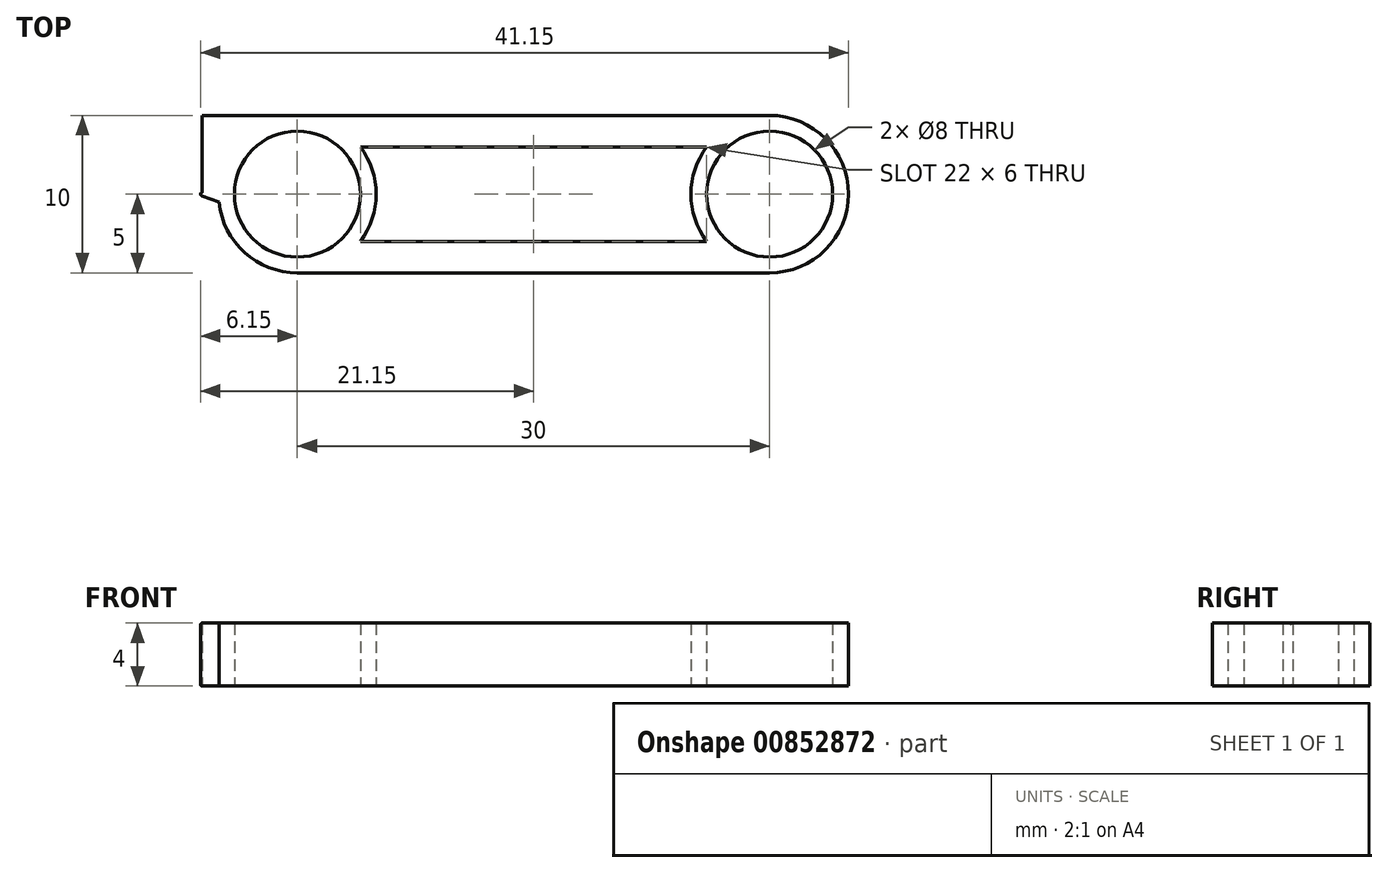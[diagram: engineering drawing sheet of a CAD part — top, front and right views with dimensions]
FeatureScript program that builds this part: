
annotation { "Feature Type Name" : "Feature", "Feature Type Description" : "" }
export const myFeature = defineFeature(function(context is Context, id is Id, definition is map)
    precondition{}
    {
        {
            var Q0;
            Q0=qCreatedBy(makeId("Top.planeOp"),FACE);
            var sketch = newSketch(context, id + "F0", { "sketchPlane" : qUnion([Q0])});
            skCircle(sketch, "E0", {"center": v(0, 0) * mm, "radius": 4 * mm});
            skArc(sketch, "E1", {"start": v(0, 5) * mm, "mid": v(-5, 0) * mm, "end": v(0, -5) * mm});
            skLineSegment(sketch, "E2", {"start": v(0, 5) * mm, "end": v(15, 5) * mm});
            skLineSegment(sketch, "E3", {"start": v(0, -5) * mm, "end": v(15, -5) * mm});
            skLineSegment(sketch, "E4", {"start": v(15, 5) * mm, "end": v(15, -5) * mm, "construction": true});
            skArc(sketch, "E5.MirrorCS", {"start": v(30, 5) * mm, "mid": v(35, 0) * mm, "end": v(30, -5) * mm});
            skCircle(sketch, "E6.MirrorC", {"center": v(30, 0) * mm, "radius": 4 * mm});
            skLineSegment(sketch, "E7.MirrorCS", {"start": v(30, -5) * mm, "end": v(15, -5) * mm});
            skLineSegment(sketch, "E8.MirrorCS", {"start": v(30, 5) * mm, "end": v(15, 5) * mm});
            skLineSegment(sketch, "E9", {"start": v(4, 3) * mm, "end": v(15, 3) * mm});
            skLineSegment(sketch, "E10.MirrorCS", {"start": v(4, -3) * mm, "end": v(15, -3) * mm});
            skArc(sketch, "E11.trimOffspring", {"start": v(4, -3) * mm, "mid": v(5, 0) * mm, "end": v(4, 3) * mm});
            skLineSegment(sketch, "E12.MirrorCS", {"start": v(26, -3) * mm, "end": v(15, -3) * mm});
            skArc(sketch, "E13.MirrorCS", {"start": v(26, -3) * mm, "mid": v(25, 0) * mm, "end": v(26, 3) * mm});
            skLineSegment(sketch, "E14.MirrorCS", {"start": v(26, 3) * mm, "end": v(15, 3) * mm});
            skSolve(sketch);
        }
        {
            var Q0;
            Q0 = qSketchRegion(id + "F0", true);
            extrude(context, id + "F1", {"entities" : qUnion([Q0]), "depth" : 4 * mm, "offsetDistance" : 25 * mm});
        }
        {
            var Q0;
            Q0=qCreatedBy(makeId("Top.planeOp"),FACE);
            var sketch = newSketch(context, id + "F2", { "sketchPlane" : qUnion([Q0])});
            skLineSegment(sketch, "E15", {"start": v(-6.35, 0) * mm, "end": v(-4.97, 0.5) * mm});
            skLineSegment(sketch, "E16.MirrorCS", {"start": v(-6.35, 0) * mm, "end": v(-4.97, -0.5) * mm});
            skLineSegment(sketch, "E17", {"start": v(-4.97, 0.5) * mm, "end": v(-4.97, -0.5) * mm});
            skLineSegment(sketch, "E18", {"start": v(-6.15, 0.07) * mm, "end": v(-6.15, -0.07) * mm});
            skSolve(sketch);
        }
        {
            var Q0;
            {var subQ6=sQuery(id+"F2.wireOp",EDGE,"E18");Q0=makeQuery(id+"F2.imprint","IMPRINT",FACE,{"disambiguationData":[TD([[makeQuery(id+"F2.imprint","IMPRINT",EDGE,{"derivedFrom":subQ6}),1.0]])]});}
            var Q1;
            Q1=makeQuery(id+"F1.opExtrude","CAP_FACE",FACE,{"disambiguationData":[OSD([sQuery(id+"F0.wireOp",EDGE,"E0"),sQuery(id+"F0.wireOp",EDGE,"E1"),sQuery(id+"F0.wireOp",EDGE,"E2"),sQuery(id+"F0.wireOp",EDGE,"E3"),sQuery(id+"F0.wireOp",EDGE,"E5.MirrorCS"),sQuery(id+"F0.wireOp",EDGE,"E6.MirrorC"),sQuery(id+"F0.wireOp",EDGE,"E7.MirrorCS"),sQuery(id+"F0.wireOp",EDGE,"E8.MirrorCS")])],"isStart":false});
            extrude(context, id + "F3", {"entities" : qUnion([Q0]), "operationType" : NewBodyOperationType.ADD, "endBound" : BoundingType.UP_TO_SURFACE, "depth" : 25 * mm, "endBoundEntityFace" : qUnion([Q1]), "offsetDistance" : 25 * mm});
        }
        {
            var Q0;
            Q0=makeQuery(id+"F3.opExtrude","SWEPT_FACE",FACE,{"disambiguationData":[OSD([sQuery(id+"F2.wireOp",EDGE,"E18")])]});
            fillet(context, id + "F4", {"entities" : qUnion([Q0]), "radius" : .1 * mm, "tangentPropagation" : true, "allowEdgeOverflow" : false});
        }
        {
            var Q0;
            Q0=qCreatedBy(makeId("Top.planeOp"),FACE);
            var sketch = newSketch(context, id + "F5", { "sketchPlane" : qUnion([Q0])});
            skArc(sketch, "E19.0", {"start": v(0, 5) * mm, "mid": v(-3.35, 3.7) * mm, "end": v(-4.97, 0.5) * mm});
            skLineSegment(sketch, "E20", {"start": v(-6.05, 5) * mm, "end": v(0, 5) * mm});
            skLineSegment(sketch, "E21.0", {"start": v(-6.05, 0.1) * mm, "end": v(-4.97, 0.5) * mm});
            skLineSegment(sketch, "E22", {"start": v(-6.05, 0.1) * mm, "end": v(-6.05, 5) * mm});
            skSolve(sketch);
        }
        {
            var Q0;
            Q0 = qSketchRegion(id + "F5", true);
            var Q1;
            {var subQ0=sQuery(id+"F0.wireOp",EDGE,"E14.MirrorCS");var subQ1=sQuery(id+"F0.wireOp",EDGE,"E13.MirrorCS");var subQ2=sQuery(id+"F0.wireOp",EDGE,"E12.MirrorCS");var subQ3=sQuery(id+"F0.wireOp",EDGE,"E11.trimOffspring");var subQ4=sQuery(id+"F0.wireOp",EDGE,"E10.MirrorCS");var subQ5=sQuery(id+"F0.wireOp",EDGE,"E9");var subQ6=sQuery(id+"F0.wireOp",EDGE,"E1");var subQ7=sQuery(id+"F0.wireOp",EDGE,"E8.MirrorCS");var subQ8=sQuery(id+"F0.wireOp",EDGE,"E7.MirrorCS");var subQ9=sQuery(id+"F0.wireOp",EDGE,"E6.MirrorC");var subQ10=sQuery(id+"F0.wireOp",EDGE,"E5.MirrorCS");var subQ11=sQuery(id+"F0.wireOp",EDGE,"E3");var subQ12=sQuery(id+"F0.wireOp",EDGE,"E2");var subQ13=sQuery(id+"F0.wireOp",EDGE,"E0");Q1=makeQuery(id+"FsRkIq0gfVC7o2m_1.7.F3.boolean.opBoolean","MERGE",FACE,{"derivedFrom":[makeQuery(id+"FsRkIq0gfVC7o2m_1.6.F3.boolean.opBoolean","MERGE",FACE,{"derivedFrom":[makeQuery(id+"FsRkIq0gfVC7o2m_1.5.F3.boolean.opBoolean","MERGE",FACE,{"derivedFrom":[makeQuery(id+"FsRkIq0gfVC7o2m_1.4.F3.boolean.opBoolean","MERGE",FACE,{"derivedFrom":[makeQuery(id+"FsRkIq0gfVC7o2m_1.3.F3.boolean.opBoolean","MERGE",FACE,{"derivedFrom":[makeQuery(id+"FsRkIq0gfVC7o2m_1.2.F3.boolean.opBoolean","MERGE",FACE,{"derivedFrom":[makeQuery(id+"FsRkIq0gfVC7o2m_1.1.F3.boolean.opBoolean","MERGE",FACE,{"derivedFrom":[makeQuery(id+"F3.boolean.opBoolean","MERGE",FACE,{"derivedFrom":[makeQuery(id+"F1.opExtrude","CAP_FACE",FACE,{"disambiguationData":[OSD([subQ13,subQ12,subQ11,subQ10,subQ9,subQ8,subQ7,subQ6,subQ5,subQ4,subQ3,subQ2,subQ1,subQ0])],"isStart":false}),makeQuery(id+"F3.opExtrude","CAP_FACE",FACE,{"disambiguationData":[OSD([subQ13,subQ12,subQ11,subQ10,subQ9,subQ8,subQ7,subQ6,subQ5,subQ4,subQ3,subQ2,subQ1,subQ0])],"isStart":false})]}),makeQuery(id+"FsRkIq0gfVC7o2m_1.1.F3.opExtrude","CAP_FACE",FACE,{"disambiguationData":[OSD([subQ13,subQ12,subQ11,subQ10,subQ9,subQ8,subQ7,subQ6,subQ5,subQ4,subQ3,subQ2,subQ1,subQ0])],"isStart":false})]}),makeQuery(id+"FsRkIq0gfVC7o2m_1.2.F3.opExtrude","CAP_FACE",FACE,{"disambiguationData":[OSD([subQ13,subQ12,subQ11,subQ10,subQ9,subQ8,subQ7,subQ6,subQ5,subQ4,subQ3,subQ2,subQ1,subQ0])],"isStart":false})]}),makeQuery(id+"FsRkIq0gfVC7o2m_1.3.F3.opExtrude","CAP_FACE",FACE,{"disambiguationData":[OSD([subQ13,subQ12,subQ11,subQ10,subQ9,subQ8,subQ7,subQ6,subQ5,subQ4,subQ3,subQ2,subQ1,subQ0])],"isStart":false})]}),makeQuery(id+"FsRkIq0gfVC7o2m_1.4.F3.opExtrude","CAP_FACE",FACE,{"disambiguationData":[OSD([subQ13,subQ12,subQ11,subQ10,subQ9,subQ8,subQ7,subQ6,subQ5,subQ4,subQ3,subQ2,subQ1,subQ0])],"isStart":false})]}),makeQuery(id+"FsRkIq0gfVC7o2m_1.5.F3.opExtrude","CAP_FACE",FACE,{"disambiguationData":[OSD([subQ13,subQ12,subQ11,subQ10,subQ9,subQ8,subQ7,subQ6,subQ5,subQ4,subQ3,subQ2,subQ1,subQ0])],"isStart":false})]}),makeQuery(id+"FsRkIq0gfVC7o2m_1.6.F3.opExtrude","CAP_FACE",FACE,{"disambiguationData":[OSD([subQ13,subQ12,subQ11,subQ10,subQ9,subQ8,subQ7,subQ6,subQ5,subQ4,subQ3,subQ2,subQ1,subQ0])],"isStart":false})]}),makeQuery(id+"FsRkIq0gfVC7o2m_1.7.F3.opExtrude","CAP_FACE",FACE,{"disambiguationData":[OSD([subQ13,subQ12,subQ11,subQ10,subQ9,subQ8,subQ7,subQ6,subQ5,subQ4,subQ3,subQ2,subQ1,subQ0])],"isStart":false})]});}
            extrude(context, id + "F6", {"entities" : qUnion([Q0]), "operationType" : NewBodyOperationType.ADD, "endBound" : BoundingType.UP_TO_SURFACE, "depth" : 25 * mm, "endBoundEntityFace" : qUnion([Q1]), "offsetDistance" : 25 * mm});
        }
    });
